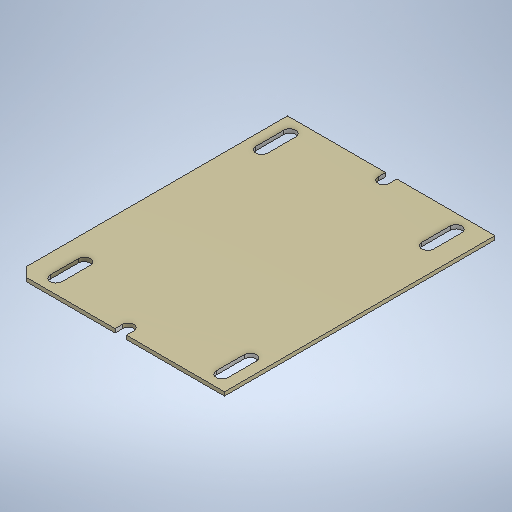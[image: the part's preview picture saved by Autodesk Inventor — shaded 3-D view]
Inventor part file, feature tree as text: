
AUTODESK INVENTOR PART (.ipt)
format: ipt  version: 2025 (Build 290162000, 162)  size: 383,488 bytes
history: native  units: in
note: dims shown in document units (in); Inventor stores cm internally (conversion verified against a paired STEP export)
features: extrude x5, sketch x3, hole x1
ambient origin geometry x8: Origin, YZ Plane, XZ Plane, XY Plane, X Axis, Y Axis, Z Axis, Center Point
bodies: Body1 (feature_tree)
feature tree (9):
  extrude  "Extrusion2"  Depth=2.2638in
  extrude  "Extrusion3"  Depth=0.0984in
  hole  "Hole1"  [1 undecoded]
  extrude  "Extrusion4"  TaperAngle=0.0deg  [1 undecoded]
  extrude  "Extrusion5"  Depth=0.0492in
  extrude  "Extrusion6"  Depth=0.0492in
  sketch  "Sketch3"  dims[d28=1.7362in d29=2.2638in]
  sketch  "Sketch6"  dims[d30=0.0315in d31=0.0in d32=0.0984in]
  sketch  "Sketch7"  dims[d33=0.3543in d34=0.0492in d35=0.0in d36=0.0in d37=0.8681in d38=0.063in d40=0.063in d41=0.0945in d42=0.1575in d43=0.1732in d44=0.0787in d45=0.6181in d46=0.315in d47=0.8108in d48=0.2087in d49=0.0787in d50=0.0787in d51=0.0in d52=0.0in d60=0.3543in d61=0.3543in d62=0.0492in d64=0.3543in d65=0.3543in d66=0.0492in d68=1.7362in d69=0.3937in d70=0.0in d71=0.1378in d73=0.0492in d74=0.0492in d75=0.1181in d76=0.3937in d77=0.0in d78=0.0492in d79=0.0492in d80=0.1181in d81=0.0492in d82=0.1181in d85=0.0492in d86=0.1181in d87=0.2087in d88=0.1378in]
note: 2 required parameter values undecoded (feature->parameter linkage not recoverable at this tier; creation-order binding heuristic only, values carry confidence <= 0.55)
